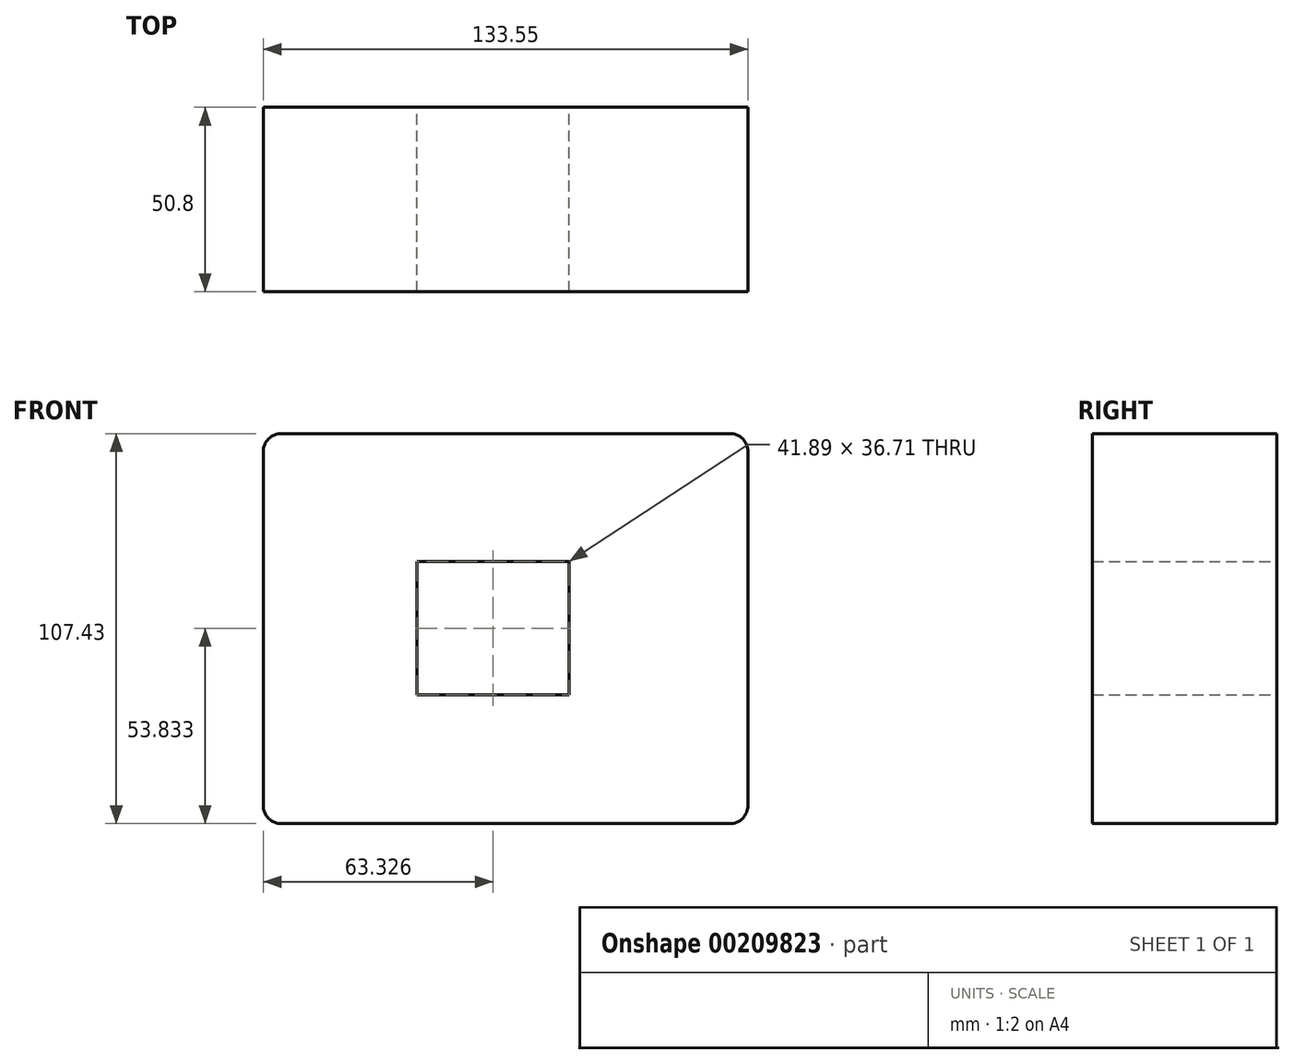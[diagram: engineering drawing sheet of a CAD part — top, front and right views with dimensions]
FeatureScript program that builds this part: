
annotation { "Feature Type Name" : "Feature", "Feature Type Description" : "" }
export const myFeature = defineFeature(function(context is Context, id is Id, definition is map)
    precondition{}
    {
        {
            var Q0;
            Q0=qCreatedBy(makeId("Front.planeOp"),FACE);
            var sketch = newSketch(context, id + "F0", { "sketchPlane" : qUnion([Q0])});
            skLineSegment(sketch, "E0.bottom", {"start": v(-108.9, 35.24) * mm, "end": v(24.64, 35.24) * mm});
            skLineSegment(sketch, "E0.top", {"start": v(-108.9, -72.2) * mm, "end": v(24.64, -72.2) * mm});
            skLineSegment(sketch, "E0.left", {"start": v(-108.9, 35.24) * mm, "end": v(-108.9, -72.2) * mm});
            skLineSegment(sketch, "E0.right", {"start": v(24.64, 35.24) * mm, "end": v(24.64, -72.2) * mm});
            skLineSegment(sketch, "E1.bottom", {"start": v(-66.53, 0) * mm, "end": v(-24.64, 0) * mm});
            skLineSegment(sketch, "E1.top", {"start": v(-66.53, -36.71) * mm, "end": v(-24.64, -36.71) * mm});
            skLineSegment(sketch, "E1.left", {"start": v(-66.53, 0) * mm, "end": v(-66.53, -36.71) * mm});
            skLineSegment(sketch, "E1.right", {"start": v(-24.64, 0) * mm, "end": v(-24.64, -36.71) * mm});
            skSolve(sketch);
        }
        {
            var Q0;
            Q0=makeQuery(id+"F0.imprint","IMPRINT",FACE,{"disambiguationData":[TD([[makeQuery(id+"F0.imprint","IMPRINT",EDGE,{"derivedFrom":sQuery(id+"F0.wireOp",EDGE,"E0.bottom")}),-1.0]])]});
            extrude(context, id + "F1", {"entities" : qUnion([Q0]), "depth" : 50.8 * mm});
        }
        {
            var Q0;
            Q0=makeQuery(id+"F1.opExtrude","SWEPT_EDGE",EDGE,{"disambiguationData":[OSD([sQuery(id+"F0.wireOp",EDGE,"E0.top"),sQuery(id+"F0.wireOp",EDGE,"E0.left")])]});
            var Q1;
            Q1=makeQuery(id+"F1.opExtrude","SWEPT_EDGE",EDGE,{"disambiguationData":[OSD([sQuery(id+"F0.wireOp",EDGE,"E0.top"),sQuery(id+"F0.wireOp",EDGE,"E0.right")])]});
            var Q2;
            Q2=makeQuery(id+"F1.opExtrude","SWEPT_EDGE",EDGE,{"disambiguationData":[OSD([sQuery(id+"F0.wireOp",EDGE,"E0.bottom"),sQuery(id+"F0.wireOp",EDGE,"E0.left")])]});
            var Q3;
            Q3=makeQuery(id+"F1.opExtrude","SWEPT_EDGE",EDGE,{"disambiguationData":[OSD([sQuery(id+"F0.wireOp",EDGE,"E0.bottom"),sQuery(id+"F0.wireOp",EDGE,"E0.right")])]});
            fillet(context, id + "F2", {"entities" : qUnion([Q0, Q1, Q2, Q3]), "radius" : 5.08 * mm, "tangentPropagation" : true, "allowEdgeOverflow" : false});
        }
    });
